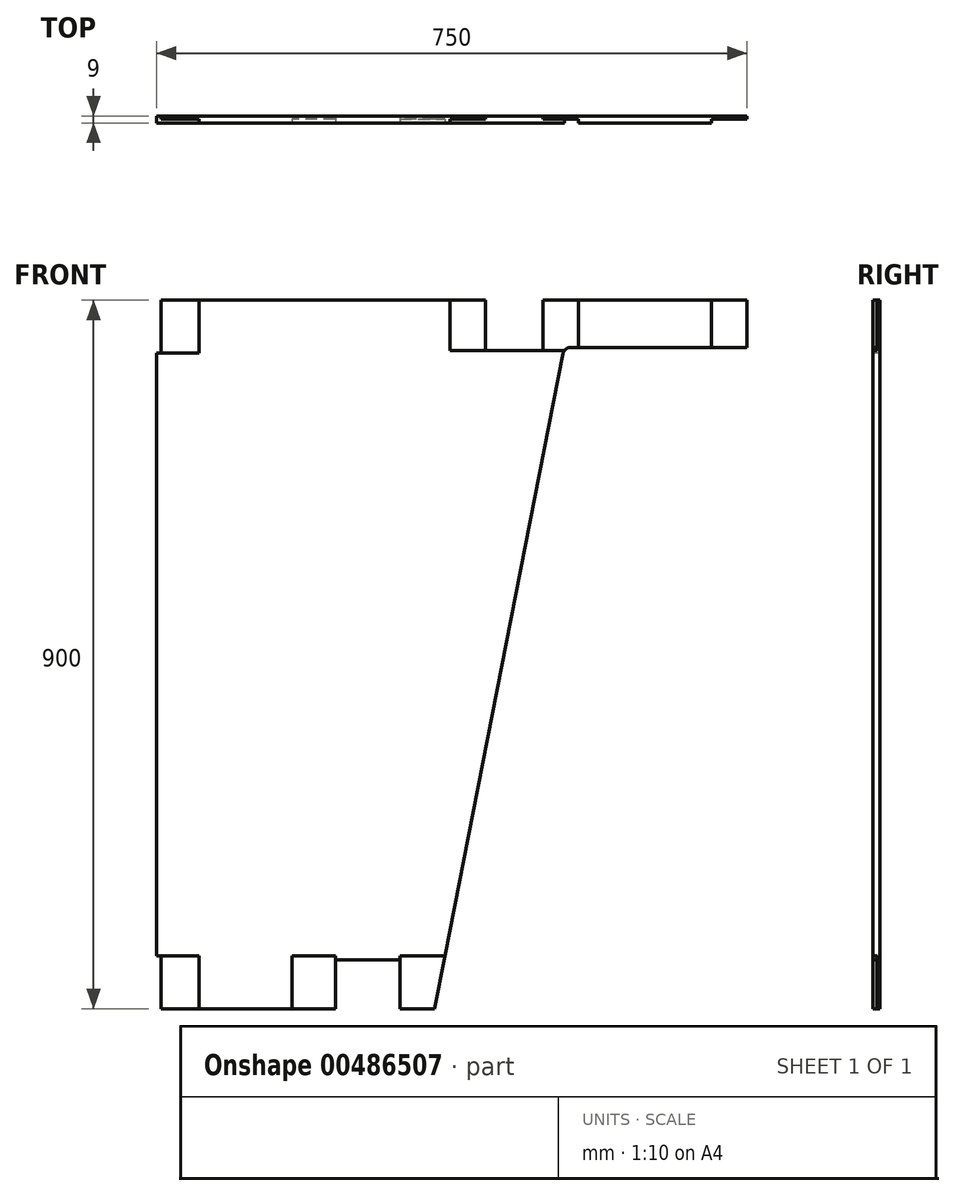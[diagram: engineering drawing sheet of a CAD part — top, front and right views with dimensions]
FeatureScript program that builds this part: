
annotation { "Feature Type Name" : "Feature", "Feature Type Description" : "" }
export const myFeature = defineFeature(function(context is Context, id is Id, definition is map)
    precondition{}
    {
        {
            var Q0;
            Q0=qCreatedBy(makeId("Front.planeOp"),FACE);
            var sketch = newSketch(context, id + "F0", { "sketchPlane" : qUnion([Q0])});
            skLineSegment(sketch, "E0", {"start": v(0, 900) * mm, "end": v(750, 900) * mm});
            skLineSegment(sketch, "E1", {"start": v(750, 900) * mm, "end": v(750, 840) * mm});
            skLineSegment(sketch, "E2", {"start": v(750, 840) * mm, "end": v(526.23, 840) * mm});
            skLineSegment(sketch, "E3", {"start": v(516.42, 831.92) * mm, "end": v(353.27, 0) * mm});
            skLineSegment(sketch, "E4", {"start": v(353.27, 0) * mm, "end": v(0, 0) * mm});
            skLineSegment(sketch, "E5", {"start": v(0, 900) * mm, "end": v(0, 0) * mm});
            skPoint(sketch, "E6.visualSharp", {"position": v(518, 840) * mm});
            skArc(sketch, "E6.filletArc", {"start": v(526.23, 840) * mm, "mid": v(519.88, 837.72) * mm, "end": v(516.42, 831.92) * mm});
            skLineSegment(sketch, "E7", {"start": v(54, 900) * mm, "end": v(54, 833) * mm});
            skLineSegment(sketch, "E8", {"start": v(54, 833) * mm, "end": v(0, 833) * mm});
            skLineSegment(sketch, "E9", {"start": v(705, 900) * mm, "end": v(705, 840) * mm});
            skLineSegment(sketch, "E10", {"start": v(491, 900) * mm, "end": v(491, 836) * mm});
            skLineSegment(sketch, "E11", {"start": v(491, 836) * mm, "end": v(418, 836) * mm});
            skLineSegment(sketch, "E12", {"start": v(418, 836) * mm, "end": v(418, 900) * mm});
            skLineSegment(sketch, "E13", {"start": v(418, 836) * mm, "end": v(373, 836) * mm});
            skLineSegment(sketch, "E14", {"start": v(373, 836) * mm, "end": v(373, 900) * mm});
            skLineSegment(sketch, "E15", {"start": v(491, 900) * mm, "end": v(536, 900) * mm});
            skLineSegment(sketch, "E16", {"start": v(536, 900) * mm, "end": v(536, 840) * mm});
            skLineSegment(sketch, "E17", {"start": v(518.23, 836) * mm, "end": v(491, 836) * mm});
            skLineSegment(sketch, "E18", {"start": v(309.27, 0) * mm, "end": v(309.27, 67) * mm});
            skLineSegment(sketch, "E19", {"start": v(309.27, 67) * mm, "end": v(366.4, 67) * mm});
            skLineSegment(sketch, "E20", {"start": v(227.27, 0) * mm, "end": v(227.27, 67) * mm});
            skLineSegment(sketch, "E21", {"start": v(227.27, 62) * mm, "end": v(309.27, 62) * mm});
            skLineSegment(sketch, "E22", {"start": v(172.27, 0) * mm, "end": v(172.27, 67) * mm});
            skLineSegment(sketch, "E23", {"start": v(172.27, 67) * mm, "end": v(227.27, 67) * mm});
            skLineSegment(sketch, "E24", {"start": v(6, 900) * mm, "end": v(6, 833) * mm});
            skLineSegment(sketch, "E25", {"start": v(0, 67) * mm, "end": v(54, 67) * mm});
            skLineSegment(sketch, "E26", {"start": v(54, 67) * mm, "end": v(54, 0) * mm});
            skLineSegment(sketch, "E27", {"start": v(6, 67) * mm, "end": v(6, 0) * mm});
            skSolve(sketch);
        }
        {
            var Q0;
            {var subQ3=sQuery(id+"F0.wireOp",EDGE,"E7");Q0=makeQuery(id+"F0.imprint","IMPRINT",FACE,{"disambiguationData":[TD([[makeQuery(id+"F0.imprint","IMPRINT",EDGE,{"derivedFrom":subQ3}),-1.0]])]});}
            var Q1;
            {var subQ0=sQuery(id+"F0.wireOp",EDGE,"E1");Q1=makeQuery(id+"F0.imprint","IMPRINT",FACE,{"disambiguationData":[TD([[makeQuery(id+"F0.imprint","IMPRINT",EDGE,{"derivedFrom":subQ0}),-1.0]])]});}
            var Q2;
            {var subQ0=sQuery(id+"F0.wireOp",EDGE,"E12");Q2=makeQuery(id+"F0.imprint","IMPRINT",FACE,{"disambiguationData":[TD([[makeQuery(id+"F0.imprint","IMPRINT",EDGE,{"derivedFrom":subQ0}),1.0]])]});}
            var Q3;
            {var subQ0=sQuery(id+"F0.wireOp",EDGE,"E9");Q3=makeQuery(id+"F0.imprint","IMPRINT",FACE,{"disambiguationData":[TD([[makeQuery(id+"F0.imprint","IMPRINT",EDGE,{"derivedFrom":subQ0}),-1.0]])]});}
            var Q4;
            {var subQ3=sQuery(id+"F0.wireOp",EDGE,"E3");Q4=makeQuery(id+"F0.imprint","IMPRINT",FACE,{"disambiguationData":[TD([[makeQuery(id+"F0.imprint","IMPRINT",EDGE,{"derivedFrom":subQ3}),-1.0]])]});}
            var Q5;
            Q5=makeQuery(id+"F0.imprint","IMPRINT",FACE,{"disambiguationData":[TD([[makeQuery(id+"F0.imprint","IMPRINT",EDGE,{"derivedFrom":sQuery(id+"F0.wireOp",EDGE,"E10")}),1.0]])]});
            var Q6;
            {var subQ1=sQuery(id+"F0.wireOp",EDGE,"E7");Q6=makeQuery(id+"F0.imprint","IMPRINT",FACE,{"disambiguationData":[TD([[makeQuery(id+"F0.imprint","IMPRINT",EDGE,{"derivedFrom":subQ1}),1.0]])]});}
            var Q7;
            {var subQ0=sQuery(id+"F0.wireOp",EDGE,"E22");Q7=makeQuery(id+"F0.imprint","IMPRINT",FACE,{"disambiguationData":[TD([[makeQuery(id+"F0.imprint","IMPRINT",EDGE,{"derivedFrom":subQ0}),-1.0]])]});}
            var Q8;
            {var subQ0=sQuery(id+"F0.wireOp",EDGE,"E26");Q8=makeQuery(id+"F0.imprint","IMPRINT",FACE,{"disambiguationData":[TD([[makeQuery(id+"F0.imprint","IMPRINT",EDGE,{"derivedFrom":subQ0}),-1.0]])]});}
            extrude(context, id + "F1", {"entities" : qUnion([Q0, Q1, Q2, Q3, Q4, Q5, Q6, Q7, Q8]), "oppositeDirection" : true, "depth" : 9 * mm, "offsetDistance" : 25 * mm});
        }
        {
            var Q0;
            {var subQ3=sQuery(id+"F0.wireOp",EDGE,"E7");Q0=makeQuery(id+"F0.imprint","IMPRINT",FACE,{"disambiguationData":[TD([[makeQuery(id+"F0.imprint","IMPRINT",EDGE,{"derivedFrom":subQ3}),-1.0]])]});}
            var Q1;
            {var subQ0=sQuery(id+"F0.wireOp",EDGE,"E1");Q1=makeQuery(id+"F0.imprint","IMPRINT",FACE,{"disambiguationData":[TD([[makeQuery(id+"F0.imprint","IMPRINT",EDGE,{"derivedFrom":subQ0}),-1.0]])]});}
            var Q2;
            {var subQ0=sQuery(id+"F0.wireOp",EDGE,"E12");Q2=makeQuery(id+"F0.imprint","IMPRINT",FACE,{"disambiguationData":[TD([[makeQuery(id+"F0.imprint","IMPRINT",EDGE,{"derivedFrom":subQ0}),1.0]])]});}
            var Q3;
            Q3=makeQuery(id+"F0.imprint","IMPRINT",FACE,{"disambiguationData":[TD([[makeQuery(id+"F0.imprint","IMPRINT",EDGE,{"derivedFrom":sQuery(id+"F0.wireOp",EDGE,"E10")}),1.0]])]});
            var Q4;
            {var subQ0=sQuery(id+"F0.wireOp",EDGE,"E19");Q4=makeQuery(id+"F0.imprint","IMPRINT",FACE,{"disambiguationData":[TD([[makeQuery(id+"F0.imprint","IMPRINT",EDGE,{"derivedFrom":subQ0}),-1.0]])]});}
            var Q5;
            {var subQ0=sQuery(id+"F0.wireOp",EDGE,"E22");Q5=makeQuery(id+"F0.imprint","IMPRINT",FACE,{"disambiguationData":[TD([[makeQuery(id+"F0.imprint","IMPRINT",EDGE,{"derivedFrom":subQ0}),-1.0]])]});}
            var Q6;
            {var subQ0=sQuery(id+"F0.wireOp",EDGE,"E26");Q6=makeQuery(id+"F0.imprint","IMPRINT",FACE,{"disambiguationData":[TD([[makeQuery(id+"F0.imprint","IMPRINT",EDGE,{"derivedFrom":subQ0}),-1.0]])]});}
            extrude(context, id + "F2", {"entities" : qUnion([Q0, Q1, Q2, Q3, Q4, Q5, Q6]), "operationType" : NewBodyOperationType.REMOVE, "oppositeDirection" : true, "depth" : 5 * mm, "offsetDistance" : 25 * mm});
        }
    });
